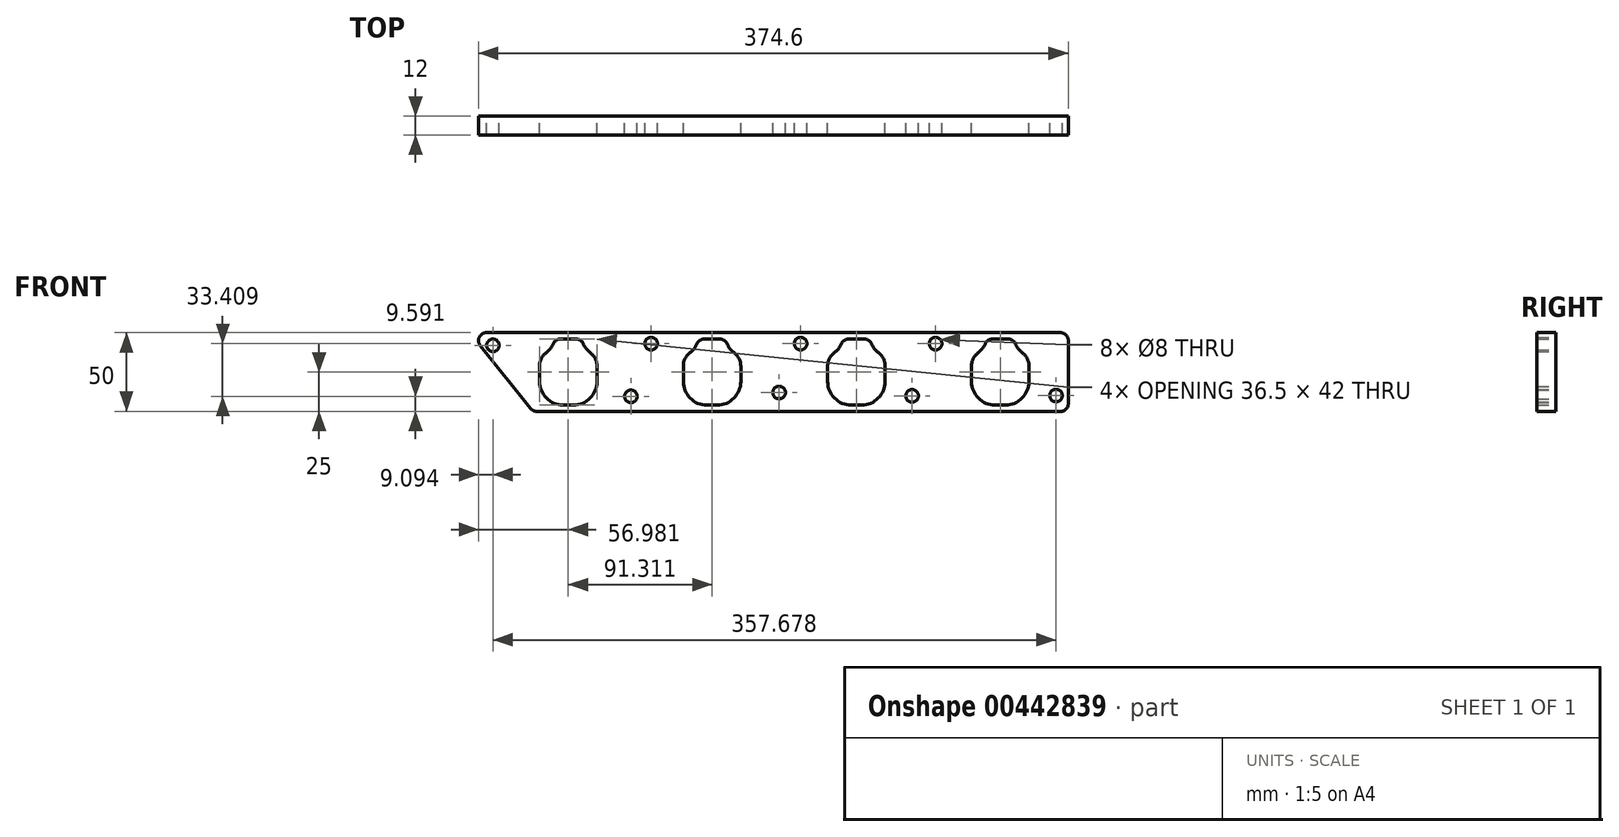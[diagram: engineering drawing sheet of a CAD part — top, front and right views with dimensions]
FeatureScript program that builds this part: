
annotation { "Feature Type Name" : "Feature", "Feature Type Description" : "" }
export const myFeature = defineFeature(function(context is Context, id is Id, definition is map)
    precondition{}
    {
        {
            var Q0;
            Q0=qCreatedBy(makeId("Front.planeOp"),FACE);
            var sketch = newSketch(context, id + "F0", { "sketchPlane" : qUnion([Q0])});
            skLineSegment(sketch, "E0", {"start": v(-181, 50) * mm, "end": v(183.6, 50) * mm});
            skLineSegment(sketch, "E1", {"start": v(188.6, 45) * mm, "end": v(188.6, 5) * mm});
            skLineSegment(sketch, "E2", {"start": v(183.6, 0) * mm, "end": v(-149, 0) * mm});
            skLineSegment(sketch, "E3", {"start": v(-184.9, 41.88) * mm, "end": v(-152.9, 1.88) * mm});
            skLineSegment(sketch, "E4", {"start": v(-151.4, 0) * mm, "end": v(-151.4, 25) * mm, "construction": true});
            skPoint(sketch, "E5.visualSharp", {"position": v(-191.4, 50) * mm});
            skArc(sketch, "E5.filletArc", {"start": v(-181, 50) * mm, "mid": v(-185.5, 47.17) * mm, "end": v(-184.9, 41.88) * mm});
            skPoint(sketch, "E6.visualSharp", {"position": v(-151.4, 0) * mm});
            skArc(sketch, "E6.filletArc", {"start": v(-152.9, 1.88) * mm, "mid": v(-151.16, 0.5) * mm, "end": v(-149, 0) * mm});
            skPoint(sketch, "E7.visualSharp", {"position": v(188.6, 50) * mm});
            skArc(sketch, "E7.filletArc", {"start": v(188.6, 45) * mm, "mid": v(187.14, 48.54) * mm, "end": v(183.6, 50) * mm});
            skPoint(sketch, "E8.visualSharp", {"position": v(188.6, 0) * mm});
            skArc(sketch, "E8.filletArc", {"start": v(183.6, 0) * mm, "mid": v(187.14, 1.46) * mm, "end": v(188.6, 5) * mm});
            skLineSegment(sketch, "E9", {"start": v(-151.4, 25) * mm, "end": v(188.6, 25) * mm, "construction": true});
            skLineSegment(sketch, "E10", {"start": v(188.6, 46) * mm, "end": v(163.6, 46) * mm, "construction": true});
            skLineSegment(sketch, "E11", {"start": v(188.6, 4) * mm, "end": v(163.6, 4) * mm, "construction": true});
            skLineSegment(sketch, "E12", {"start": v(167.71, 0) * mm, "end": v(167.71, 4) * mm, "construction": true});
            skLineSegment(sketch, "E13", {"start": v(163.6, 29) * mm, "end": v(163.6, 19) * mm, "construction": true});
            skLineSegment(sketch, "E14", {"start": v(150.28, 46) * mm, "end": v(140.44, 46) * mm});
            skLineSegment(sketch, "E15", {"start": v(148.6, 4) * mm, "end": v(142.1, 4) * mm});
            skLineSegment(sketch, "E16", {"start": v(127.1, 29) * mm, "end": v(127.1, 19) * mm});
            skLineSegment(sketch, "E17", {"start": v(163.6, 46) * mm, "end": v(163.6, 4) * mm});
            skPoint(sketch, "E18.visualSharp", {"position": v(127.1, 4) * mm});
            skArc(sketch, "E18.filletArc", {"start": v(127.1, 19) * mm, "mid": v(131.5, 8.4) * mm, "end": v(142.1, 4) * mm});
            skPoint(sketch, "E19.visualSharp", {"position": v(163.6, 4) * mm});
            skArc(sketch, "E19.filletArc", {"start": v(148.6, 4) * mm, "mid": v(159.21, 8.4) * mm, "end": v(163.6, 19) * mm});
            skLineSegment(sketch, "E20", {"start": v(127.1, 4) * mm, "end": v(127.1, 34) * mm});
            skLineSegment(sketch, "E21", {"start": v(137.1, 39) * mm, "end": v(153.6, 39) * mm});
            skArc(sketch, "E22.filletArc", {"start": v(131.1, 37) * mm, "mid": v(128.16, 33.47) * mm, "end": v(127.1, 29) * mm});
            skArc(sketch, "E23.filletArc", {"start": v(163.6, 29) * mm, "mid": v(162.55, 33.47) * mm, "end": v(159.6, 37) * mm});
            skLineSegment(sketch, "E24", {"start": v(137.1, 46) * mm, "end": v(137.1, 49) * mm});
            skLineSegment(sketch, "E25", {"start": v(153.6, 46) * mm, "end": v(153.6, 49) * mm});
            skPoint(sketch, "E26.visualSharp", {"position": v(137.1, 39) * mm});
            skArc(sketch, "E26.filletArc", {"start": v(131.1, 37) * mm, "mid": v(133.87, 39.7) * mm, "end": v(135.85, 43) * mm});
            skPoint(sketch, "E27.visualSharp", {"position": v(153.6, 39) * mm});
            skArc(sketch, "E27.filletArc", {"start": v(154.86, 43) * mm, "mid": v(156.84, 39.7) * mm, "end": v(159.6, 37) * mm});
            skPoint(sketch, "E28.newPointA", {"position": v(127.1, 46) * mm});
            skArc(sketch, "E28.filletArc", {"start": v(140.44, 46) * mm, "mid": v(137.7, 45.18) * mm, "end": v(135.85, 43) * mm});
            skPoint(sketch, "E29.newPointA", {"position": v(163.6, 46) * mm});
            skArc(sketch, "E29.filletArc", {"start": v(154.86, 43) * mm, "mid": v(153.01, 45.18) * mm, "end": v(150.28, 46) * mm});
            skPoint(sketch, "E30.endSnap0", {"position": v(133.87, 39.7) * mm});
            skLineSegment(sketch, "E31", {"start": v(127.1, 19) * mm, "end": v(72.1, 19) * mm, "construction": true});
            skLineSegment(sketch, "E32", {"start": v(72.25, 29) * mm, "end": v(72.25, 19) * mm, "construction": true});
            skLineSegment(sketch, "E33", {"start": v(58.92, 46) * mm, "end": v(49.08, 46) * mm});
            skLineSegment(sketch, "E34", {"start": v(57.25, 4) * mm, "end": v(50.75, 4) * mm});
            skLineSegment(sketch, "E35", {"start": v(35.75, 29) * mm, "end": v(35.75, 19) * mm});
            skLineSegment(sketch, "E36", {"start": v(72.25, 46) * mm, "end": v(72.25, 4) * mm});
            skPoint(sketch, "E37.visualSharp", {"position": v(35.75, 4) * mm});
            skArc(sketch, "E37.filletArc", {"start": v(35.75, 19) * mm, "mid": v(40.15, 8.4) * mm, "end": v(50.75, 4) * mm});
            skPoint(sketch, "E38.visualSharp", {"position": v(72.25, 4) * mm});
            skArc(sketch, "E38.filletArc", {"start": v(57.25, 4) * mm, "mid": v(67.86, 8.4) * mm, "end": v(72.25, 19) * mm});
            skLineSegment(sketch, "E39", {"start": v(35.75, 4) * mm, "end": v(35.75, 34) * mm});
            skLineSegment(sketch, "E40", {"start": v(45.75, 39) * mm, "end": v(62.25, 39) * mm});
            skArc(sketch, "E41.filletArc", {"start": v(39.75, 37) * mm, "mid": v(36.8, 33.47) * mm, "end": v(35.75, 29) * mm});
            skArc(sketch, "E42.filletArc", {"start": v(72.25, 29) * mm, "mid": v(71.2, 33.47) * mm, "end": v(68.25, 37) * mm});
            skPoint(sketch, "E43.visualSharp", {"position": v(45.75, 39) * mm});
            skArc(sketch, "E43.filletArc", {"start": v(39.75, 37) * mm, "mid": v(42.51, 39.7) * mm, "end": v(44.5, 43) * mm});
            skPoint(sketch, "E44.visualSharp", {"position": v(62.25, 39) * mm});
            skArc(sketch, "E44.filletArc", {"start": v(63.5, 43) * mm, "mid": v(65.49, 39.7) * mm, "end": v(68.25, 37) * mm});
            skPoint(sketch, "E45.newPointA", {"position": v(35.75, 46) * mm});
            skArc(sketch, "E45.filletArc", {"start": v(49.08, 46) * mm, "mid": v(46.34, 45.18) * mm, "end": v(44.5, 43) * mm});
            skPoint(sketch, "E46.newPointA", {"position": v(72.25, 46) * mm});
            skArc(sketch, "E46.filletArc", {"start": v(63.5, 43) * mm, "mid": v(61.66, 45.18) * mm, "end": v(58.92, 46) * mm});
            skPoint(sketch, "E47.endSnap0", {"position": v(42.51, 39.7) * mm});
            skLineSegment(sketch, "E48", {"start": v(35.75, 4) * mm, "end": v(-172.04, 4) * mm, "construction": true});
            skLineSegment(sketch, "E49", {"start": v(35.75, 19) * mm, "end": v(-19.25, 19) * mm, "construction": true});
            skLineSegment(sketch, "E50", {"start": v(-19.45, 29) * mm, "end": v(-19.45, 19) * mm, "construction": true});
            skLineSegment(sketch, "E51", {"start": v(-32.78, 46) * mm, "end": v(-42.62, 46) * mm});
            skLineSegment(sketch, "E52", {"start": v(-34.45, 4) * mm, "end": v(-40.95, 4) * mm});
            skLineSegment(sketch, "E53", {"start": v(-55.95, 29) * mm, "end": v(-55.95, 19) * mm});
            skLineSegment(sketch, "E54", {"start": v(-19.45, 46) * mm, "end": v(-19.45, 4) * mm});
            skPoint(sketch, "E55.visualSharp", {"position": v(-55.95, 4) * mm});
            skArc(sketch, "E55.filletArc", {"start": v(-55.95, 19) * mm, "mid": v(-51.55, 8.4) * mm, "end": v(-40.95, 4) * mm});
            skPoint(sketch, "E56.visualSharp", {"position": v(-19.45, 4) * mm});
            skArc(sketch, "E56.filletArc", {"start": v(-34.45, 4) * mm, "mid": v(-23.84, 8.4) * mm, "end": v(-19.45, 19) * mm});
            skLineSegment(sketch, "E57", {"start": v(-55.95, 4) * mm, "end": v(-55.95, 34) * mm});
            skLineSegment(sketch, "E58", {"start": v(-45.95, 39) * mm, "end": v(-29.45, 39) * mm});
            skArc(sketch, "E59.filletArc", {"start": v(-51.95, 37) * mm, "mid": v(-54.9, 33.47) * mm, "end": v(-55.95, 29) * mm});
            skArc(sketch, "E60.filletArc", {"start": v(-19.45, 29) * mm, "mid": v(-20.5, 33.47) * mm, "end": v(-23.45, 37) * mm});
            skPoint(sketch, "E61.visualSharp", {"position": v(-45.95, 39) * mm});
            skArc(sketch, "E61.filletArc", {"start": v(-51.95, 37) * mm, "mid": v(-49.18, 39.7) * mm, "end": v(-47.2, 43) * mm});
            skPoint(sketch, "E62.visualSharp", {"position": v(-29.45, 39) * mm});
            skArc(sketch, "E62.filletArc", {"start": v(-28.2, 43) * mm, "mid": v(-26.21, 39.7) * mm, "end": v(-23.45, 37) * mm});
            skPoint(sketch, "E63.newPointA", {"position": v(-55.95, 46) * mm});
            skArc(sketch, "E63.filletArc", {"start": v(-42.62, 46) * mm, "mid": v(-45.36, 45.18) * mm, "end": v(-47.2, 43) * mm});
            skPoint(sketch, "E64.newPointA", {"position": v(-19.45, 46) * mm});
            skArc(sketch, "E64.filletArc", {"start": v(-28.2, 43) * mm, "mid": v(-30.04, 45.18) * mm, "end": v(-32.78, 46) * mm});
            skPoint(sketch, "E65.endSnap0", {"position": v(-49.18, 39.7) * mm});
            skLineSegment(sketch, "E66", {"start": v(-55.95, 19) * mm, "end": v(-110.95, 19) * mm, "construction": true});
            skLineSegment(sketch, "E67", {"start": v(-110.76, 29) * mm, "end": v(-110.76, 19) * mm, "construction": true});
            skLineSegment(sketch, "E68", {"start": v(-124.09, 46) * mm, "end": v(-133.93, 46) * mm});
            skLineSegment(sketch, "E69", {"start": v(-125.76, 4) * mm, "end": v(-132.26, 4) * mm});
            skLineSegment(sketch, "E70", {"start": v(-147.26, 29) * mm, "end": v(-147.26, 19) * mm});
            skLineSegment(sketch, "E71", {"start": v(-110.76, 46) * mm, "end": v(-110.76, 4) * mm});
            skPoint(sketch, "E72.visualSharp", {"position": v(-147.26, 4) * mm});
            skArc(sketch, "E72.filletArc", {"start": v(-147.26, 19) * mm, "mid": v(-142.87, 8.4) * mm, "end": v(-132.26, 4) * mm});
            skPoint(sketch, "E73.visualSharp", {"position": v(-110.76, 4) * mm});
            skArc(sketch, "E73.filletArc", {"start": v(-125.76, 4) * mm, "mid": v(-115.15, 8.4) * mm, "end": v(-110.76, 19) * mm});
            skLineSegment(sketch, "E74", {"start": v(-147.26, 4) * mm, "end": v(-147.26, 34) * mm});
            skLineSegment(sketch, "E75", {"start": v(-137.26, 39) * mm, "end": v(-120.76, 39) * mm});
            skArc(sketch, "E76.filletArc", {"start": v(-143.26, 37) * mm, "mid": v(-146.2, 33.47) * mm, "end": v(-147.26, 29) * mm});
            skArc(sketch, "E77.filletArc", {"start": v(-110.76, 29) * mm, "mid": v(-111.81, 33.47) * mm, "end": v(-114.76, 37) * mm});
            skPoint(sketch, "E78.visualSharp", {"position": v(-137.26, 39) * mm});
            skArc(sketch, "E78.filletArc", {"start": v(-143.26, 37) * mm, "mid": v(-140.5, 39.7) * mm, "end": v(-138.51, 43) * mm});
            skPoint(sketch, "E79.visualSharp", {"position": v(-120.76, 39) * mm});
            skArc(sketch, "E79.filletArc", {"start": v(-119.5, 43) * mm, "mid": v(-117.52, 39.7) * mm, "end": v(-114.76, 37) * mm});
            skPoint(sketch, "E80.newPointA", {"position": v(-147.26, 46) * mm});
            skArc(sketch, "E80.filletArc", {"start": v(-133.93, 46) * mm, "mid": v(-136.67, 45.18) * mm, "end": v(-138.51, 43) * mm});
            skPoint(sketch, "E81.newPointA", {"position": v(-110.76, 46) * mm});
            skArc(sketch, "E81.filletArc", {"start": v(-119.5, 43) * mm, "mid": v(-121.35, 45.18) * mm, "end": v(-124.09, 46) * mm});
            skPoint(sketch, "E82.endSnap0", {"position": v(-140.5, 39.7) * mm});
            skLineSegment(sketch, "E83", {"start": v(-176.9, 42) * mm, "end": v(-176.9, 50) * mm, "construction": true});
            skLineSegment(sketch, "E84", {"start": v(-176.9, 42) * mm, "end": v(-184.9, 41.88) * mm, "construction": true});
            skCircle(sketch, "E85", {"center": v(-176.9, 42) * mm, "radius": 4 * mm});
            skCircle(sketch, "E86", {"center": v(-76.37, 43) * mm, "radius": 4 * mm});
            skCircle(sketch, "E87", {"center": v(-89.26, 9.6) * mm, "radius": 4 * mm});
            skCircle(sketch, "E88", {"center": v(18.55, 43) * mm, "radius": 4 * mm});
            skCircle(sketch, "E89", {"center": v(4.9, 11.97) * mm, "radius": 4 * mm});
            skCircle(sketch, "E90", {"center": v(104.27, 43) * mm, "radius": 4 * mm});
            skCircle(sketch, "E91", {"center": v(89.35, 9.88) * mm, "radius": 4 * mm});
            skCircle(sketch, "E92", {"center": v(180.78, 10.07) * mm, "radius": 4 * mm});
            skSolve(sketch);
        }
        {
            var Q0;
            Q0=makeQuery(id+"F0.imprint","IMPRINT",FACE,{"disambiguationData":[TD([[makeQuery(id+"F0.imprint","IMPRINT",EDGE,{"derivedFrom":sQuery(id+"F0.wireOp",EDGE,"E0")}),-1.0]])]});
            extrude(context, id + "F1", {"entities" : qUnion([Q0]), "depth" : 12 * mm});
        }
        {
            var Q0;
            Q0=qCreatedBy(makeId("Front.planeOp"),FACE);
            cPlane(context, id + "F2", {"entities" : qUnion([Q0]), "cplaneType" : CPlaneType.OFFSET, "offset" : 200 * mm, "oppositeDirection" : true, "width" : 150 * mm, "height" : 150 * mm});
        }
    });
